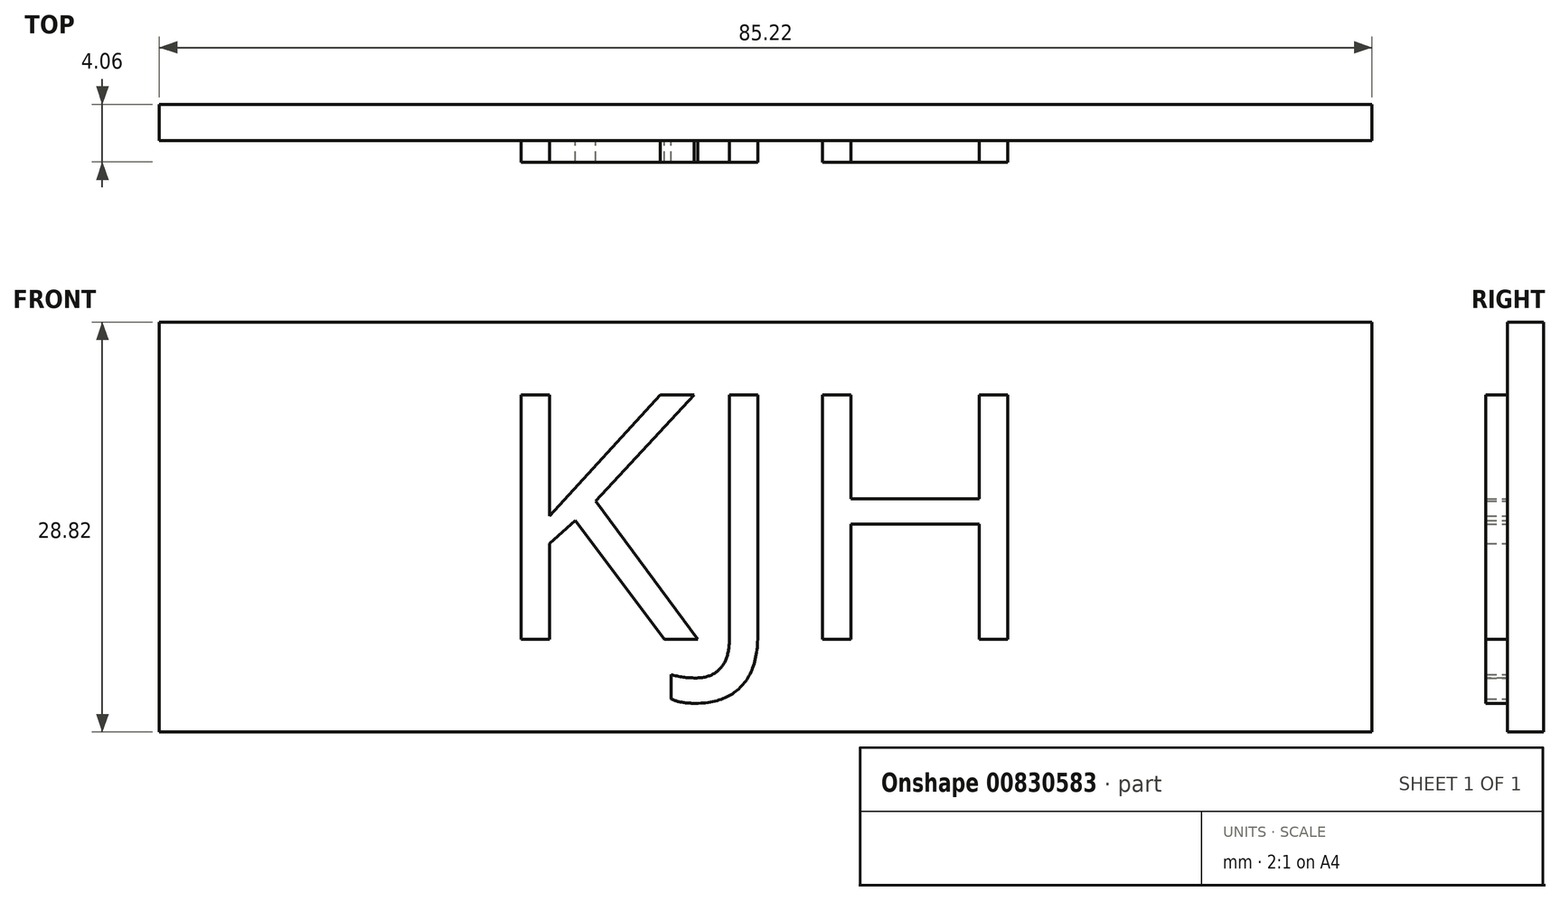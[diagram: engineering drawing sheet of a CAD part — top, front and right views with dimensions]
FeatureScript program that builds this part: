
annotation { "Feature Type Name" : "Feature", "Feature Type Description" : "" }
export const myFeature = defineFeature(function(context is Context, id is Id, definition is map)
    precondition{}
    {
        {
            var Q0;
            Q0=qCreatedBy(makeId("Front.planeOp"),FACE);
            var sketch = newSketch(context, id + "F0", { "sketchPlane" : qUnion([Q0])});
            skLineSegment(sketch, "E0.bottom", {"start": v(0, 0) * mm, "end": v(85.22, 0) * mm});
            skLineSegment(sketch, "E0.top", {"start": v(0, 28.82) * mm, "end": v(85.22, 28.82) * mm});
            skLineSegment(sketch, "E0.left", {"start": v(0, 0) * mm, "end": v(0, 28.82) * mm});
            skLineSegment(sketch, "E0.right", {"start": v(85.22, 0) * mm, "end": v(85.22, 28.82) * mm});
            skSolve(sketch);
        }
        {
            var Q0;
            Q0=makeQuery(id+"F0.imprint","IMPRINT",FACE,{"disambiguationData":[TD([[makeQuery(id+"F0.imprint","IMPRINT",EDGE,{"derivedFrom":sQuery(id+"F0.wireOp",EDGE,"E0.bottom")}),1.0]])]});
            extrude(context, id + "F1", {"entities" : qUnion([Q0]), "depth" : 2.54 * mm, "offsetDistance" : 25.4 * mm});
        }
        {
            var Q0;
            Q0=makeQuery(id+"F1.opExtrude","CAP_FACE",FACE,{"disambiguationData":[OSD([sQuery(id+"F0.wireOp",EDGE,"E0.bottom"),sQuery(id+"F0.wireOp",EDGE,"E0.top"),sQuery(id+"F0.wireOp",EDGE,"E0.left"),sQuery(id+"F0.wireOp",EDGE,"E0.right")])],"isStart":false});
            var sketch = newSketch(context, id + "F2", { "sketchPlane" : qUnion([Q0])});
            skText(sketch, "E1", { "text": "KJH", "fontName": "OpenSans-Regular.ttf"});
            const initialGuessF2  = {"E1": [0.02308, 0.00654, 1, 0, 0.0173]};
            skSetInitialGuess(sketch, initialGuessF2);
            skSolve(sketch);
        }
        {
            var Q0;
            Q0 = qSketchRegion(id + "F2", true);
            extrude(context, id + "F3", {"entities" : qUnion([Q0]), "operationType" : NewBodyOperationType.ADD, "depth" : 1.52 * mm, "offsetDistance" : 25.4 * mm});
        }
    });
